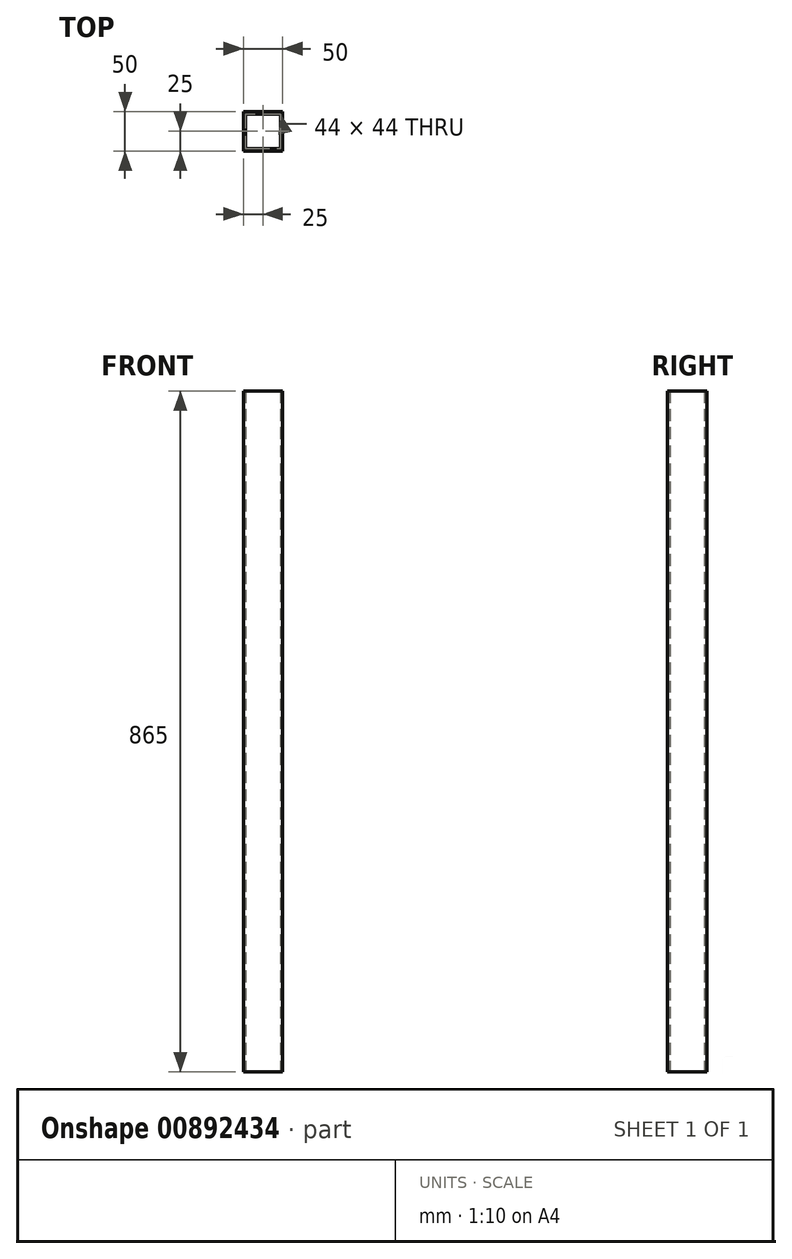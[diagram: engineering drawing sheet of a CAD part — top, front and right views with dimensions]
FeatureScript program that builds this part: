
annotation { "Feature Type Name" : "Feature", "Feature Type Description" : "" }
export const myFeature = defineFeature(function(context is Context, id is Id, definition is map)
    precondition{}
    {
        {
            var Q0;
            Q0=qCreatedBy(makeId("Top.planeOp"),FACE);
            var sketch = newSketch(context, id + "F0", { "sketchPlane" : qUnion([Q0])});
            skLineSegment(sketch, "E0.bottom", {"start": v(25, -25) * mm, "end": v(-25, -25) * mm});
            skLineSegment(sketch, "E0.top", {"start": v(25, 25) * mm, "end": v(-25, 25) * mm});
            skLineSegment(sketch, "E0.left", {"start": v(25, -25) * mm, "end": v(25, 25) * mm});
            skLineSegment(sketch, "E0.right", {"start": v(-25, -25) * mm, "end": v(-25, 25) * mm});
            skPoint(sketch, "E0.middle", {"position": v(0, 0) * mm});
            skLineSegment(sketch, "E1.0", {"start": v(22, 22) * mm, "end": v(-22, 22) * mm});
            skLineSegment(sketch, "E1.1", {"start": v(22, -22) * mm, "end": v(22, 22) * mm});
            skLineSegment(sketch, "E1.2", {"start": v(22, -22) * mm, "end": v(-22, -22) * mm});
            skLineSegment(sketch, "E1.3", {"start": v(-22, -22) * mm, "end": v(-22, 22) * mm});
            skSolve(sketch);
        }
        {
            var Q0;
            Q0=makeQuery(id+"F0.imprint","IMPRINT",FACE,{"disambiguationData":[TD([[makeQuery(id+"F0.imprint","IMPRINT",EDGE,{"derivedFrom":sQuery(id+"F0.wireOp",EDGE,"E0.bottom")}),-1.0]])]});
            extrude(context, id + "F1", {"entities" : qUnion([Q0]), "depth" : 865 * mm, "offsetDistance" : 25 * mm});
        }
    });
